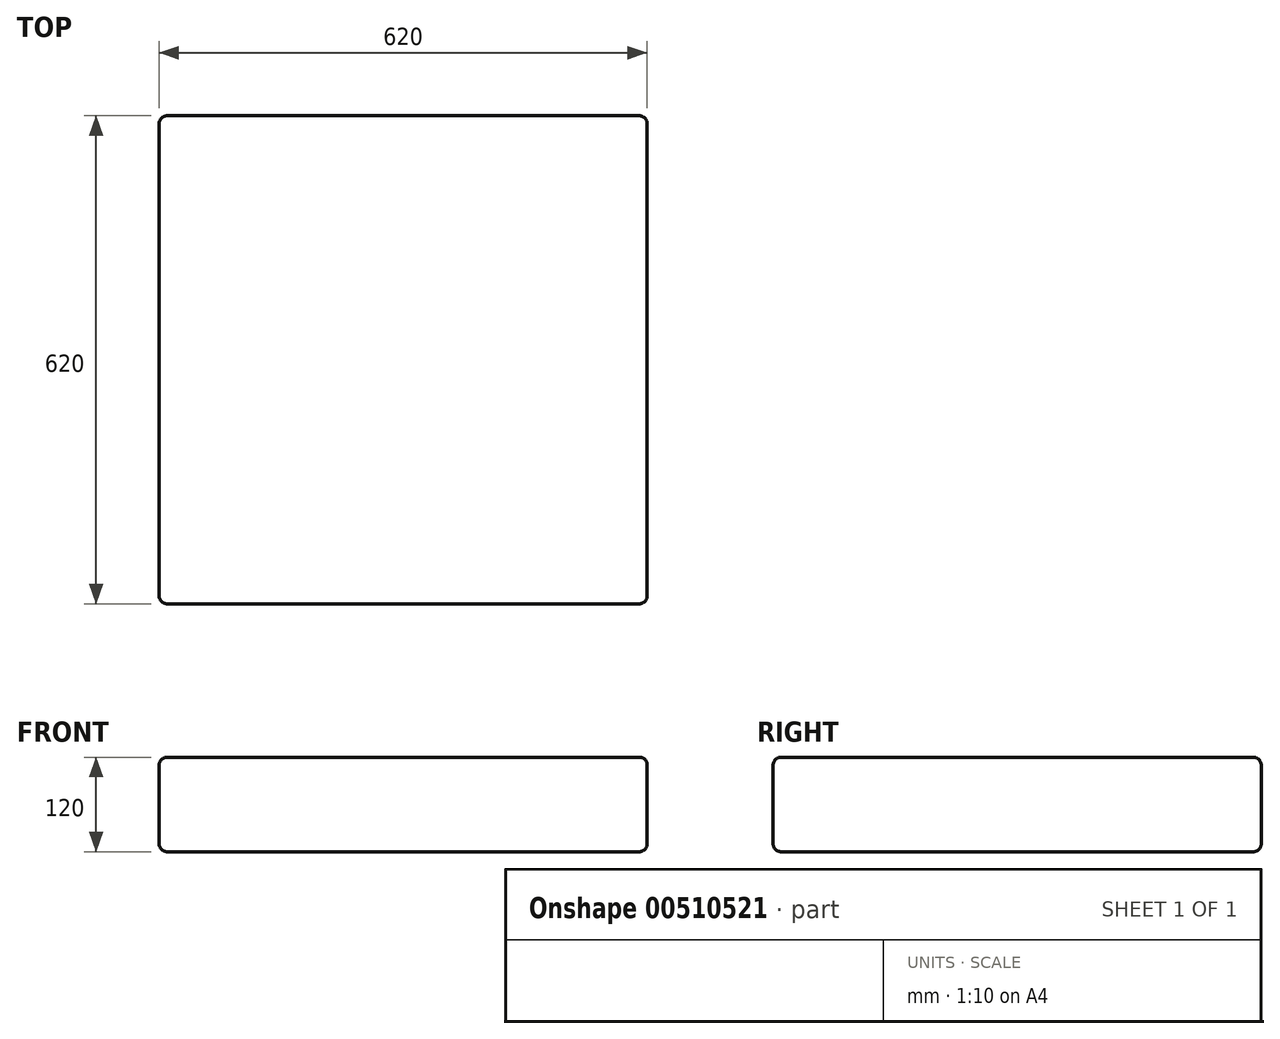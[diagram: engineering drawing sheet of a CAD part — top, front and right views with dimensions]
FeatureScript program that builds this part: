
annotation { "Feature Type Name" : "Feature", "Feature Type Description" : "" }
export const myFeature = defineFeature(function(context is Context, id is Id, definition is map)
    precondition{}
    {
        {
            var Q0;
            Q0=qCreatedBy(makeId("Top.planeOp"),FACE);
            var sketch = newSketch(context, id + "F0", { "sketchPlane" : qUnion([Q0])});
            skLineSegment(sketch, "E0.bottom", {"start": v(0, 0) * mm, "end": v(620, 0) * mm});
            skLineSegment(sketch, "E0.top", {"start": v(0, 620) * mm, "end": v(620, 620) * mm});
            skLineSegment(sketch, "E0.left", {"start": v(0, 0) * mm, "end": v(0, 620) * mm});
            skLineSegment(sketch, "E0.right", {"start": v(620, 0) * mm, "end": v(620, 620) * mm});
            skSolve(sketch);
        }
        {
            var Q0;
            Q0 = qSketchRegion(id + "F0", true);
            extrude(context, id + "F1", {"entities" : qUnion([Q0]), "depth" : 120 * mm, "offsetDistance" : 25 * mm});
        }
        {
            var Q0;
            Q0=makeQuery(id+"F1.opExtrude","SWEPT_EDGE",EDGE,{"disambiguationData":[OSD([sQuery(id+"F0.wireOp",EDGE,"E0.bottom"),sQuery(id+"F0.wireOp",EDGE,"E0.right")])]});
            var Q1;
            Q1=makeQuery(id+"F1.opExtrude","SWEPT_EDGE",EDGE,{"disambiguationData":[OSD([sQuery(id+"F0.wireOp",EDGE,"E0.top"),sQuery(id+"F0.wireOp",EDGE,"E0.right")])]});
            var Q2;
            Q2=makeQuery(id+"F1.opExtrude","SWEPT_EDGE",EDGE,{"disambiguationData":[OSD([sQuery(id+"F0.wireOp",EDGE,"E0.bottom"),sQuery(id+"F0.wireOp",EDGE,"E0.left")])]});
            var Q3;
            Q3=makeQuery(id+"F1.opExtrude","SWEPT_EDGE",EDGE,{"disambiguationData":[OSD([sQuery(id+"F0.wireOp",EDGE,"E0.top"),sQuery(id+"F0.wireOp",EDGE,"E0.left")])]});
            fillet(context, id + "F2", {"entities" : qUnion([Q0, Q1, Q2, Q3]), "radius" : 10 * mm, "tangentPropagation" : true, "allowEdgeOverflow" : false});
        }
        {
            var Q0;
            Q0=makeQuery(id+"F1.opExtrude","CAP_EDGE",EDGE,{"disambiguationData":[OSD([sQuery(id+"F0.wireOp",EDGE,"E0.bottom")])],"isStart":false});
            var Q1;
            Q1=makeQuery(id+"F1.opExtrude","CAP_EDGE",EDGE,{"disambiguationData":[OSD([sQuery(id+"F0.wireOp",EDGE,"E0.bottom")])],"isStart":true});
            fillet(context, id + "F3", {"entities" : qUnion([Q0, Q1]), "radius" : 10 * mm, "tangentPropagation" : true, "allowEdgeOverflow" : false});
        }
    });
